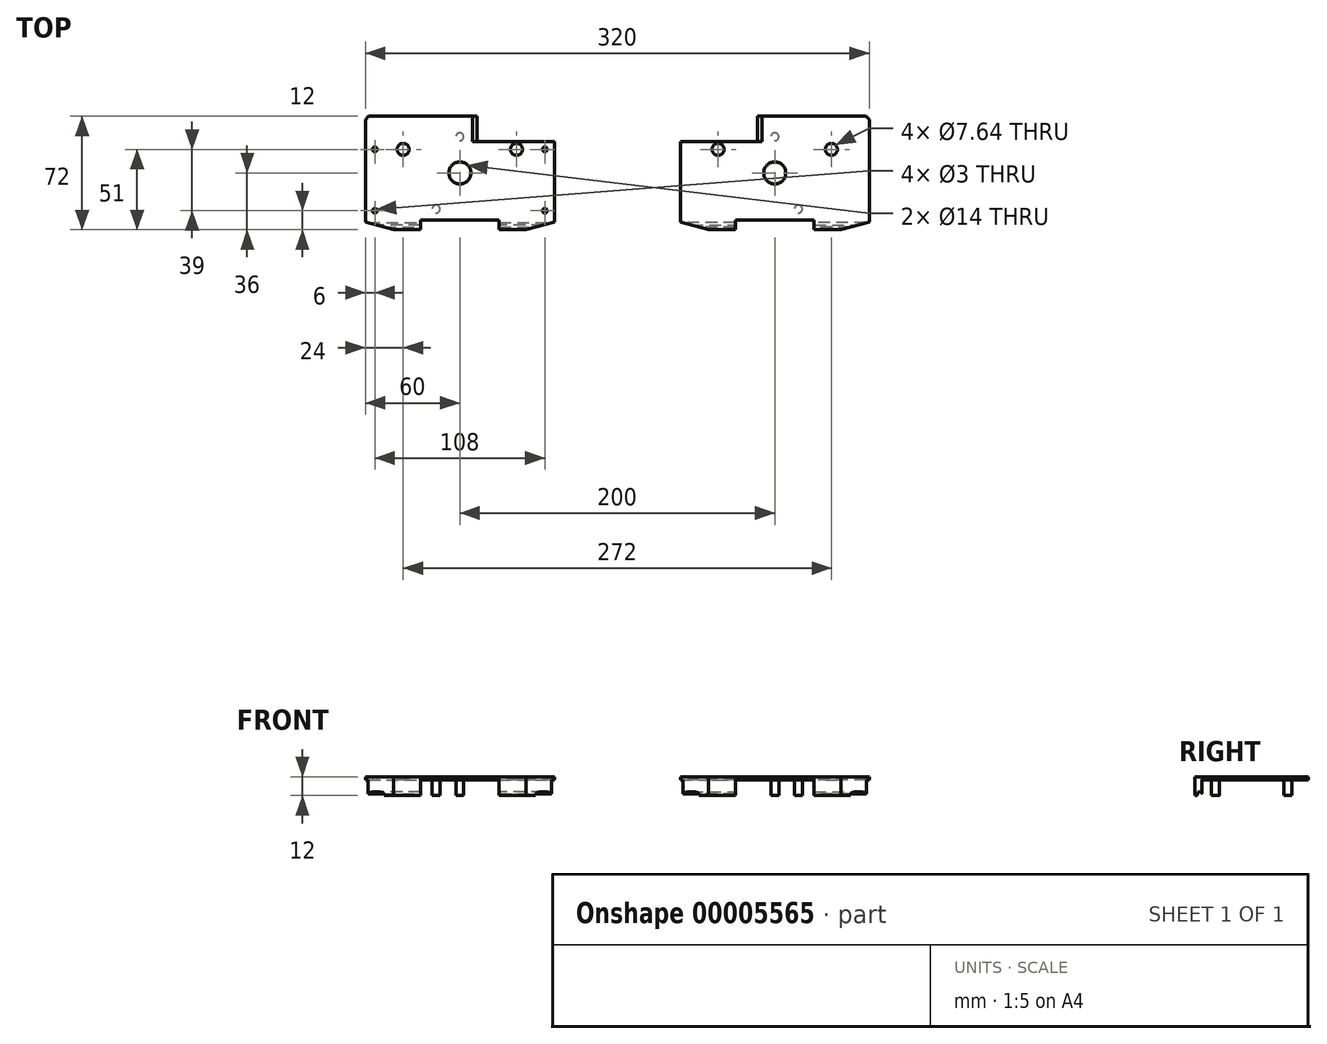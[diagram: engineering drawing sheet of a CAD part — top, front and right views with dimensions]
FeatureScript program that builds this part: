
annotation { "Feature Type Name" : "Feature", "Feature Type Description" : "" }
export const myFeature = defineFeature(function(context is Context, id is Id, definition is map)
    precondition{}
    {
        {
            var Q0;
            Q0=qCreatedBy(makeId("Top.planeOp"),FACE);
            var sketch = newSketch(context, id + "F0", { "sketchPlane" : qUnion([Q0])});
            skLineSegment(sketch, "E0.bottom", {"start": v(-60, 36) * mm, "end": v(60, 36) * mm});
            skLineSegment(sketch, "E0.top", {"start": v(-60, -36) * mm, "end": v(60, -36) * mm});
            skLineSegment(sketch, "E0.left", {"start": v(-60, 36) * mm, "end": v(-60, -36) * mm, "construction": true});
            skLineSegment(sketch, "E0.right", {"start": v(60, 36) * mm, "end": v(60, -36) * mm, "construction": true});
            skCircle(sketch, "E1", {"center": v(0, 0) * mm, "radius": 7 * mm});
            skLineSegment(sketch, "E2", {"start": v(-60, 0) * mm, "end": v(60, 0) * mm, "construction": true});
            skCircle(sketch, "E3", {"center": v(0, 23) * mm, "radius": 2.4 * mm, "construction": true});
            skCircle(sketch, "E4.0.MirrorC", {"center": v(0, -23) * mm, "radius": 2.4 * mm, "construction": true});
            skCircle(sketch, "E5.0.MirrorC", {"center": v(-15, 23) * mm, "radius": 2.5 * mm, "construction": true});
            skCircle(sketch, "E6.0.MirrorC", {"center": v(-15, -23) * mm, "radius": 2.5 * mm, "construction": true});
            skLineSegment(sketch, "E7.bottom", {"start": v(-22.32, 36) * mm, "end": v(10.24, 36) * mm, "construction": true});
            skLineSegment(sketch, "E7.top", {"start": v(-23.32, -36) * mm, "end": v(9.24, -36) * mm, "construction": true});
            skLineSegment(sketch, "E8.left", {"start": v(-60, 36) * mm, "end": v(-60, -36) * mm});
            skLineSegment(sketch, "E8.right", {"start": v(60, 36) * mm, "end": v(60, -36) * mm});
            skLineSegment(sketch, "E9.bottom", {"start": v(-60, 36) * mm, "end": v(-42, 36) * mm, "construction": true});
            skLineSegment(sketch, "E9.top", {"start": v(-60, -36) * mm, "end": v(-42, -36) * mm, "construction": true});
            skLineSegment(sketch, "E9.right", {"start": v(-42, 36) * mm, "end": v(-42, -36) * mm, "construction": true});
            skCircle(sketch, "E10", {"center": v(-36, 15) * mm, "radius": 3.82 * mm});
            skCircle(sketch, "E11.0.MirrorC", {"center": v(36, 15) * mm, "radius": 3.82 * mm});
            skLineSegment(sketch, "E12.bottom", {"start": v(10, -36) * mm, "end": v(-10, -36) * mm});
            skLineSegment(sketch, "E13", {"start": v(0, 23) * mm, "end": v(0, -23) * mm, "construction": true});
            skLineSegment(sketch, "E14", {"start": v(-36, 15) * mm, "end": v(0, 15) * mm, "construction": true});
            skLineSegment(sketch, "E15", {"start": v(0, 15) * mm, "end": v(36, 15) * mm, "construction": true});
            skCircle(sketch, "E16", {"center": v(-54, -24) * mm, "radius": 1.5 * mm, "construction": true});
            skCircle(sketch, "E17", {"center": v(-54, 15) * mm, "radius": 1.5 * mm, "construction": true});
            skLineSegment(sketch, "E18", {"start": v(-36, 15) * mm, "end": v(-56.54, 15) * mm, "construction": true});
            skLineSegment(sketch, "E19", {"start": v(-54, -24) * mm, "end": v(-54, 15) * mm, "construction": true});
            skCircle(sketch, "E20.0.MirrorC", {"center": v(54, 15) * mm, "radius": 1.5 * mm, "construction": true});
            skCircle(sketch, "E21.0.MirrorC", {"center": v(54, -24) * mm, "radius": 1.5 * mm, "construction": true});
            skSolve(sketch);
        }
        {
            var Q0;
            Q0=makeQuery(id+"F0.imprint","IMPRINT",FACE,{"disambiguationData":[TD([[makeQuery(id+"F0.imprint","IMPRINT",EDGE,{"derivedFrom":sQuery(id+"F0.wireOp",EDGE,"E1")}),-1.0]])]});
            extrude(context, id + "F1", {"entities" : qUnion([Q0]), "depth" : 12 * mm});
        }
        {
            var Q0;
            Q0=makeQuery(id+"F1.opExtrude","CAP_FACE",FACE,{"disambiguationData":[OSD([sQuery(id+"F0.wireOp",EDGE,"E1"),sQuery(id+"F0.wireOp",EDGE,"E0.bottom"),sQuery(id+"F0.wireOp",EDGE,"E0.top"),sQuery(id+"F0.wireOp",EDGE,"E8.left"),sQuery(id+"F0.wireOp",EDGE,"E8.right"),sQuery(id+"F0.wireOp",EDGE,"E10"),sQuery(id+"F0.wireOp",EDGE,"E11.0.MirrorC"),sQuery(id+"F0.wireOp",EDGE,"E12.bottom")])],"isStart":false});
            var sketch = newSketch(context, id + "F2", { "sketchPlane" : qUnion([Q0])});
            skLineSegment(sketch, "E22", {"start": v(60, 20) * mm, "end": v(60, 36) * mm});
            skLineSegment(sketch, "E23", {"start": v(60, 36) * mm, "end": v(-42, 36) * mm});
            skLineSegment(sketch, "E24", {"start": v(-60, -36) * mm, "end": v(60, -36) * mm});
            skLineSegment(sketch, "E25", {"start": v(-42, 20) * mm, "end": v(60, 20) * mm});
            skLineSegment(sketch, "E26", {"start": v(60, -36) * mm, "end": v(-60, -36) * mm});
            skLineSegment(sketch, "E27", {"start": v(-60, 36) * mm, "end": v(-42, 36) * mm, "construction": true});
            skLineSegment(sketch, "E28", {"start": v(60, 36) * mm, "end": v(60, 20) * mm});
            skLineSegment(sketch, "E29", {"start": v(-42, 36) * mm, "end": v(-42, 27) * mm, "construction": true});
            skLineSegment(sketch, "E30", {"start": v(-42, 27) * mm, "end": v(-46, 27) * mm, "construction": true});
            skLineSegment(sketch, "E31", {"start": v(-46, 27) * mm, "end": v(-46, 20) * mm, "construction": true});
            skLineSegment(sketch, "E32", {"start": v(-46, 20) * mm, "end": v(-42, 20) * mm, "construction": true});
            skSolve(sketch);
        }
        {
            var Q0;
            Q0=makeQuery(id+"F0.imprint","IMPRINT",FACE,{"disambiguationData":[TD([[makeQuery(id+"F0.imprint","IMPRINT",EDGE,{"derivedFrom":sQuery(id+"F0.wireOp",EDGE,"E1")}),-1.0]])]});
            var sketch = newSketch(context, id + "F3", { "sketchPlane" : qUnion([Q0])});
            skLineSegment(sketch, "E33.bottom", {"start": v(25, -36) * mm, "end": v(-25, -36) * mm});
            skLineSegment(sketch, "E33.top", {"start": v(25, -30) * mm, "end": v(-25, -30) * mm});
            skLineSegment(sketch, "E33.left", {"start": v(25, -36) * mm, "end": v(25, -30) * mm});
            skLineSegment(sketch, "E33.right", {"start": v(-25, -36) * mm, "end": v(-25, -30) * mm});
            skLineSegment(sketch, "E34", {"start": v(-25, -33) * mm, "end": v(0, -33) * mm, "construction": true});
            skLineSegment(sketch, "E35", {"start": v(0, -33) * mm, "end": v(25, -33) * mm, "construction": true});
            skLineSegment(sketch, "E36", {"start": v(0, -22.48) * mm, "end": v(0, -36) * mm, "construction": true});
            skSolve(sketch);
        }
        {
            var Q0;
            Q0=makeQuery(id+"F3.imprint","IMPRINT",FACE,{"disambiguationData":[TD([[makeQuery(id+"F3.imprint","IMPRINT",EDGE,{"derivedFrom":sQuery(id+"F3.wireOp",EDGE,"E33.top")}),1.0]])]});
            var Q1;
            Q1=makeQuery(id+"F1.opExtrude","CAP_FACE",FACE,{"disambiguationData":[OSD([sQuery(id+"F0.wireOp",EDGE,"E1"),sQuery(id+"F0.wireOp",EDGE,"E0.bottom"),sQuery(id+"F0.wireOp",EDGE,"E0.top"),sQuery(id+"F0.wireOp",EDGE,"E8.left"),sQuery(id+"F0.wireOp",EDGE,"E8.right"),sQuery(id+"F0.wireOp",EDGE,"E10"),sQuery(id+"F0.wireOp",EDGE,"E11.0.MirrorC"),sQuery(id+"F0.wireOp",EDGE,"E12.bottom")])],"isStart":false});
            extrude(context, id + "F4", {"entities" : qUnion([Q0]), "operationType" : NewBodyOperationType.REMOVE, "endBound" : BoundingType.UP_TO_SURFACE, "endBoundEntityFace" : qUnion([Q1]), "depth" : 25 * mm});
        }
        {
            var Q0;
            Q0=makeQuery(id+"F0.imprint","IMPRINT",FACE,{"disambiguationData":[TD([[makeQuery(id+"F0.imprint","IMPRINT",EDGE,{"derivedFrom":sQuery(id+"F0.wireOp",EDGE,"E1")}),-1.0]])]});
            var sketch = newSketch(context, id + "F5", { "sketchPlane" : qUnion([Q0])});
            skLineSegment(sketch, "E37.bottom", {"start": v(-60, -31.62) * mm, "end": v(60, -31.63) * mm});
            skLineSegment(sketch, "E37.top", {"start": v(-60, -34.37) * mm, "end": v(60, -34.38) * mm});
            skLineSegment(sketch, "E37.left", {"start": v(-60, -31.62) * mm, "end": v(-60, -34.37) * mm});
            skLineSegment(sketch, "E37.right", {"start": v(60, -31.63) * mm, "end": v(60, -34.38) * mm});
            skLineSegment(sketch, "E38", {"start": v(8.47, -31.63) * mm, "end": v(8.47, -30) * mm, "construction": true});
            skLineSegment(sketch, "E39", {"start": v(8.43, -34.38) * mm, "end": v(8.43, -36) * mm, "construction": true});
            skSolve(sketch);
        }
        {
            var Q0;
            Q0=makeQuery(id+"F5.imprint","IMPRINT",FACE,{"disambiguationData":[TD([[makeQuery(id+"F5.imprint","IMPRINT",EDGE,{"derivedFrom":sQuery(id+"F5.wireOp",EDGE,"E37.bottom")}),-1.0]])]});
            extrude(context, id + "F6", {"entities" : qUnion([Q0]), "operationType" : NewBodyOperationType.REMOVE, "depth" : 2.5 * mm});
        }
        {
            var Q0;
            Q0=makeQuery(id+"F6.boolean.opBoolean","COPY",EDGE,{"disambiguationData":[OD(1.0)],"derivedFrom":makeQuery(id+"F6.opExtrude","CAP_EDGE",EDGE,{"disambiguationData":[OSD([sQuery(id+"F5.wireOp",EDGE,"E37.bottom")])],"isStart":false})});
            var Q1;
            Q1=makeQuery(id+"F6.boolean.opBoolean","COPY",EDGE,{"disambiguationData":[OD(1.0)],"derivedFrom":makeQuery(id+"F6.opExtrude","CAP_EDGE",EDGE,{"disambiguationData":[OSD([sQuery(id+"F5.wireOp",EDGE,"E37.top")])],"isStart":false})});
            var Q2;
            Q2=makeQuery(id+"F6.boolean.opBoolean","COPY",EDGE,{"disambiguationData":[OD(0.0)],"derivedFrom":makeQuery(id+"F6.opExtrude","CAP_EDGE",EDGE,{"disambiguationData":[OSD([sQuery(id+"F5.wireOp",EDGE,"E37.top")])],"isStart":false})});
            var Q3;
            Q3=makeQuery(id+"F6.boolean.opBoolean","COPY",EDGE,{"disambiguationData":[OD(0.0)],"derivedFrom":makeQuery(id+"F6.opExtrude","CAP_EDGE",EDGE,{"disambiguationData":[OSD([sQuery(id+"F5.wireOp",EDGE,"E37.bottom")])],"isStart":false})});
            fillet(context, id + "F7", {"entities" : qUnion([Q0, Q1, Q2, Q3]), "radius" : 1.5 * mm, "tangentPropagation" : true, "allowEdgeOverflow" : false});
        }
        {
            var Q0;
            Q0=makeQuery(id+"F1.opExtrude","SWEPT_FACE",FACE,{"disambiguationData":[OSD([sQuery(id+"F0.wireOp",EDGE,"E0.bottom")])]});
            var sketch = newSketch(context, id + "F8", { "sketchPlane" : qUnion([Q0])});
            skLineSegment(sketch, "E40", {"start": v(-60, 6) * mm, "end": v(-38.5, 6) * mm, "construction": true});
            skLineSegment(sketch, "E41", {"start": v(0, 0) * mm, "end": v(0, 12) * mm, "construction": true});
            skLineSegment(sketch, "E42", {"start": v(-8, 0) * mm, "end": v(-8, 12) * mm, "construction": true});
            skLineSegment(sketch, "E43", {"start": v(-8, 12) * mm, "end": v(-60, 12) * mm});
            skLineSegment(sketch, "E44", {"start": v(-60, 2) * mm, "end": v(-60, 12) * mm});
            skLineSegment(sketch, "E45", {"start": v(-8, 2) * mm, "end": v(-23.25, 2) * mm, "construction": true});
            skLineSegment(sketch, "E46", {"start": v(-23.25, 2) * mm, "end": v(-38.5, 2) * mm, "construction": true});
            skLineSegment(sketch, "E47", {"start": v(-38.5, 6) * mm, "end": v(-38.5, 0) * mm, "construction": true});
            skLineSegment(sketch, "E48", {"start": v(-60, 2) * mm, "end": v(-23.25, 2) * mm});
            skLineSegment(sketch, "E49", {"start": v(-23.25, 2) * mm, "end": v(-8, 12) * mm});
            skSolve(sketch);
        }
        {
            var Q0;
            Q0=makeQuery(id+"F8.imprint","IMPRINT",FACE,{"disambiguationData":[TD([[makeQuery(id+"F8.imprint","IMPRINT",EDGE,{"derivedFrom":sQuery(id+"F8.wireOp",EDGE,"E43")}),1.0]])]});
            extrude(context, id + "F9", {"entities" : qUnion([Q0]), "operationType" : NewBodyOperationType.REMOVE, "oppositeDirection" : true, "depth" : 16 * mm});
        }
        {
            var Q0;
            Q0=makeQuery(id+"F9.boolean.opBoolean","COPY",EDGE,{"derivedFrom":makeQuery(id+"F9.opExtrude","SWEPT_EDGE",EDGE,{"disambiguationData":[OSD([sQuery(id+"F8.wireOp",EDGE,"dc820323-19ea-4039-b468-714fe8b4bf2b"),sQuery(id+"F8.wireOp",EDGE,"f9c62189-2ec5-4655-88e0-a14efa9e9823")])]})});
            var Q1;
            Q1=makeQuery(id+"F9.boolean.opBoolean","COPY",EDGE,{"derivedFrom":makeQuery(id+"F9.opExtrude","SWEPT_EDGE",EDGE,{"disambiguationData":[OSD([sQuery(id+"F2.wireOp",EDGE,"E23"),sQuery(id+"F8.wireOp",EDGE,"f9c62189-2ec5-4655-88e0-a14efa9e9823"),sQuery(id+"F8.wireOp",EDGE,"E43")])]})});
            var Q2;
            Q2=makeQuery(id+"F9.boolean.opBoolean","COPY",EDGE,{"derivedFrom":makeQuery(id+"F9.opExtrude","SWEPT_EDGE",EDGE,{"disambiguationData":[OSD([sQuery(id+"F8.wireOp",EDGE,"E48"),sQuery(id+"F8.wireOp",EDGE,"E49")])]})});
            var Q3;
            Q3=makeQuery(id+"F9.boolean.opBoolean","COPY",EDGE,{"derivedFrom":makeQuery(id+"F9.opExtrude","SWEPT_EDGE",EDGE,{"disambiguationData":[OSD([sQuery(id+"F0.wireOp",EDGE,"E0.bottom"),sQuery(id+"F8.wireOp",EDGE,"E43"),sQuery(id+"F8.wireOp",EDGE,"E49")])]})});
            fillet(context, id + "F10", {"entities" : qUnion([Q0, Q1, Q2, Q3]), "radius" : 5 * mm, "tangentPropagation" : true, "allowEdgeOverflow" : false});
        }
        {
            var Q0;
            {var subQ0=sQuery(id+"F0.wireOp",EDGE,"E1");var subQ1=sQuery(id+"F0.wireOp",EDGE,"E0.bottom");var subQ2=sQuery(id+"F0.wireOp",EDGE,"E8.left");var subQ3=sQuery(id+"F0.wireOp",EDGE,"E8.right");var subQ4=sQuery(id+"F0.wireOp",EDGE,"E10");var subQ5=sQuery(id+"F0.wireOp",EDGE,"E11.0.MirrorC");Q0=makeQuery(id+"F6.boolean.opBoolean","SPLIT",FACE,{"disambiguationData":[TD([makeQuery(id+"F1.opExtrude","SWEPT_FACE",FACE,{"disambiguationData":[OSD([subQ0])]}),makeQuery(id+"F1.opExtrude","SWEPT_FACE",FACE,{"disambiguationData":[OSD([subQ1])]}),makeQuery(id+"F1.opExtrude","SWEPT_FACE",FACE,{"disambiguationData":[OSD([subQ2])]}),makeQuery(id+"F1.opExtrude","SWEPT_FACE",FACE,{"disambiguationData":[OSD([subQ3])]}),makeQuery(id+"F1.opExtrude","SWEPT_FACE",FACE,{"disambiguationData":[OSD([subQ4])]}),makeQuery(id+"F1.opExtrude","SWEPT_FACE",FACE,{"disambiguationData":[OSD([subQ5])]}),makeQuery(id+"F4.boolean.opBoolean","COPY",FACE,{"derivedFrom":makeQuery(id+"F4.opExtrude","SWEPT_FACE",FACE,{"disambiguationData":[OSD([sQuery(id+"F3.wireOp",EDGE,"E33.top")])]})}),makeQuery(id+"F4.boolean.opBoolean","COPY",FACE,{"derivedFrom":makeQuery(id+"F4.opExtrude","SWEPT_FACE",FACE,{"disambiguationData":[OSD([sQuery(id+"F3.wireOp",EDGE,"E33.left")])]})}),makeQuery(id+"F4.boolean.opBoolean","COPY",FACE,{"derivedFrom":makeQuery(id+"F4.opExtrude","SWEPT_FACE",FACE,{"disambiguationData":[OSD([sQuery(id+"F3.wireOp",EDGE,"E33.right")])]})}),makeQuery(id+"F6.opExtrude","SWEPT_FACE",FACE,{"disambiguationData":[OSD([sQuery(id+"F5.wireOp",EDGE,"E37.bottom")])]})])],"derivedFrom":makeQuery(id+"F1.opExtrude","CAP_FACE",FACE,{"disambiguationData":[OSD([subQ0,subQ1,sQuery(id+"F0.wireOp",EDGE,"E0.top"),subQ2,subQ3,subQ4,subQ5,sQuery(id+"F0.wireOp",EDGE,"E12.bottom")])],"isStart":true})});}
            var sketch = newSketch(context, id + "F11", { "sketchPlane" : qUnion([Q0])});
            skCircle(sketch, "E50", {"center": v(-15.05, -22.91) * mm, "radius": 2.5 * mm});
            skCircle(sketch, "E51.0.MirrorC", {"center": v(-0.05, -23) * mm, "radius": 2.5 * mm});
            skCircle(sketch, "E52.0.MirrorC", {"center": v(-15.05, 22.91) * mm, "radius": 2.5 * mm});
            skCircle(sketch, "E53.0.MirrorC", {"center": v(-0.05, 23) * mm, "radius": 2.5 * mm});
            skSolve(sketch);
        }
        {
            var Q0;
            {Q0=qUnion([makeQuery(id+"F11.imprint","IMPRINT",FACE,{"disambiguationData":[TD([[makeQuery(id+"F11.imprint","IMPRINT",EDGE,{"derivedFrom":sQuery(id+"F11.wireOp",EDGE,"E50")}),1.0]])]}),makeQuery(id+"F11.imprint","IMPRINT",FACE,{"disambiguationData":[TD([[makeQuery(id+"F11.imprint","IMPRINT",EDGE,{"derivedFrom":sQuery(id+"F11.wireOp",EDGE,"E51.0.MirrorC")}),-1.0]])]}),makeQuery(id+"F11.imprint","IMPRINT",FACE,{"disambiguationData":[TD([[makeQuery(id+"F11.imprint","IMPRINT",EDGE,{"derivedFrom":sQuery(id+"F11.wireOp",EDGE,"E52.0.MirrorC")}),-1.0]])]}),makeQuery(id+"F11.imprint","IMPRINT",FACE,{"disambiguationData":[TD([[makeQuery(id+"F11.imprint","IMPRINT",EDGE,{"derivedFrom":sQuery(id+"F11.wireOp",EDGE,"E53.0.MirrorC")}),1.0]])]})]);}
            extrude(context, id + "F12", {"entities" : qUnion([Q0]), "operationType" : NewBodyOperationType.REMOVE, "oppositeDirection" : true, "depth" : 10 * mm});
        }
        {
            var Q0;
            Q0=makeQuery(id+"F0.imprint","IMPRINT",FACE,{"disambiguationData":[TD([[makeQuery(id+"F0.imprint","IMPRINT",EDGE,{"derivedFrom":sQuery(id+"F0.wireOp",EDGE,"E1")}),-1.0]])]});
            var sketch = newSketch(context, id + "F13", { "sketchPlane" : qUnion([Q0])});
            skLineSegment(sketch, "E54", {"start": v(-60, -31.12) * mm, "end": v(-42, -36) * mm});
            skLineSegment(sketch, "E55", {"start": v(-42, -36) * mm, "end": v(-60, -36) * mm});
            skLineSegment(sketch, "E56", {"start": v(-60, -36) * mm, "end": v(-60, -31.12) * mm});
            skPoint(sketch, "E57", {"position": v(-60, -31.62) * mm});
            skLineSegment(sketch, "E58.MirrorCS", {"start": v(60, -31.12) * mm, "end": v(42, -36) * mm});
            skLineSegment(sketch, "E59.MirrorCS", {"start": v(60, -36) * mm, "end": v(60, -31.12) * mm});
            skLineSegment(sketch, "E60.MirrorCS", {"start": v(42, -36) * mm, "end": v(60, -36) * mm});
            skSolve(sketch);
        }
        {
            var Q0;
            Q0 = qSketchRegion(id + "F13", true);
            var Q1;
            Q1=makeQuery(id+"F1.opExtrude","CAP_FACE",FACE,{"disambiguationData":[OSD([sQuery(id+"F0.wireOp",EDGE,"E1"),sQuery(id+"F0.wireOp",EDGE,"E0.bottom"),sQuery(id+"F0.wireOp",EDGE,"E0.top"),sQuery(id+"F0.wireOp",EDGE,"E8.left"),sQuery(id+"F0.wireOp",EDGE,"E8.right"),sQuery(id+"F0.wireOp",EDGE,"E10"),sQuery(id+"F0.wireOp",EDGE,"E11.0.MirrorC"),sQuery(id+"F0.wireOp",EDGE,"E12.bottom")])],"isStart":false});
            extrude(context, id + "F14", {"entities" : qUnion([Q0]), "operationType" : NewBodyOperationType.REMOVE, "endBound" : BoundingType.UP_TO_SURFACE, "endBoundEntityFace" : qUnion([Q1]), "depth" : 25 * mm});
        }
        {
            var Q0;
            Q0=makeQuery(id+"F1.opExtrude","SWEPT_EDGE",EDGE,{"disambiguationData":[OSD([sQuery(id+"F0.wireOp",EDGE,"E0.bottom"),sQuery(id+"F0.wireOp",EDGE,"E8.left")])]});
            chamfer(context, id + "F15", {"entities" : qUnion([Q0]), "width" : 2 * mm, "tangentPropagation" : true});
        }
        {
            var Q0;
            Q0=qCreatedBy(makeId("Right.planeOp"),FACE);
            cPlane(context, id + "F16", {"entities" : qUnion([Q0]), "cplaneType" : CPlaneType.OFFSET, "offset" : 100 * mm, "width" : 150 * mm, "height" : 150 * mm});
        }
        {
            var Q0;
            Q0=makeQuery(id+"F1.opExtrude","SWEPT_BODY",BODY,{"disambiguationData":[OSD([sQuery(id+"F0.wireOp",EDGE,"E1"),sQuery(id+"F0.wireOp",EDGE,"E0.bottom"),sQuery(id+"F0.wireOp",EDGE,"E0.top"),sQuery(id+"F0.wireOp",EDGE,"E8.left"),sQuery(id+"F0.wireOp",EDGE,"E8.right"),sQuery(id+"F0.wireOp",EDGE,"E10"),sQuery(id+"F0.wireOp",EDGE,"E11.0.MirrorC"),sQuery(id+"F0.wireOp",EDGE,"E12.bottom")])]});
            var Q1;
            Q1=qCreatedBy(id+"F16.planeOp",FACE);
            mirror(context, id + "F17", {"entities" : qUnion([Q0]), "mirrorPlane" : qUnion([Q1])});
        }
        {
            var Q0;
            Q0=qCreatedBy(makeId("Top.planeOp"),FACE);
            var sketch = newSketch(context, id + "F18", { "sketchPlane" : qUnion([Q0])});
            skCircle(sketch, "E61", {"center": v(-54, -24) * mm, "radius": 1.5 * mm});
            skCircle(sketch, "E62", {"center": v(-54, 15) * mm, "radius": 1.5 * mm});
            skCircle(sketch, "E63", {"center": v(54, 15) * mm, "radius": 1.5 * mm});
            skCircle(sketch, "E64", {"center": v(54, -24) * mm, "radius": 1.5 * mm});
            skSolve(sketch);
        }
        {
            var Q0;
            {Q0=qUnion([makeQuery(id+"F18.imprint","IMPRINT",FACE,{"disambiguationData":[TD([[makeQuery(id+"F18.imprint","IMPRINT",EDGE,{"derivedFrom":sQuery(id+"F18.wireOp",EDGE,"E61")}),1.0]])]}),makeQuery(id+"F18.imprint","IMPRINT",FACE,{"disambiguationData":[TD([[makeQuery(id+"F18.imprint","IMPRINT",EDGE,{"derivedFrom":sQuery(id+"F18.wireOp",EDGE,"E62")}),1.0]])]}),makeQuery(id+"F18.imprint","IMPRINT",FACE,{"disambiguationData":[TD([[makeQuery(id+"F18.imprint","IMPRINT",EDGE,{"derivedFrom":sQuery(id+"F18.wireOp",EDGE,"E63")}),1.0]])]}),makeQuery(id+"F18.imprint","IMPRINT",FACE,{"disambiguationData":[TD([[makeQuery(id+"F18.imprint","IMPRINT",EDGE,{"derivedFrom":sQuery(id+"F18.wireOp",EDGE,"E64")}),1.0]])]})]);}
            var Q1;
            Q1=makeQuery(id+"F1.opExtrude","CAP_FACE",FACE,{"disambiguationData":[OSD([sQuery(id+"F0.wireOp",EDGE,"E1"),sQuery(id+"F0.wireOp",EDGE,"E0.bottom"),sQuery(id+"F0.wireOp",EDGE,"E0.top"),sQuery(id+"F0.wireOp",EDGE,"E8.left"),sQuery(id+"F0.wireOp",EDGE,"E8.right"),sQuery(id+"F0.wireOp",EDGE,"E10"),sQuery(id+"F0.wireOp",EDGE,"E11.0.MirrorC"),sQuery(id+"F0.wireOp",EDGE,"E12.bottom")])],"isStart":false});
            extrude(context, id + "F19", {"entities" : qUnion([Q0]), "operationType" : NewBodyOperationType.REMOVE, "endBound" : BoundingType.UP_TO_SURFACE, "endBoundEntityFace" : qUnion([Q1]), "depth" : 25 * mm});
        }
        {
            var Q0;
            Q0=qCreatedBy(makeId("Top.planeOp"),FACE);
            var sketch = newSketch(context, id + "F20", { "sketchPlane" : qUnion([Q0])});
            skCircle(sketch, "E65", {"center": v(-54, -24) * mm, "radius": 3 * mm});
            skCircle(sketch, "E66", {"center": v(-54, 15) * mm, "radius": 3 * mm});
            skCircle(sketch, "E67", {"center": v(54, 15) * mm, "radius": 3 * mm});
            skCircle(sketch, "E68", {"center": v(54, -24) * mm, "radius": 3 * mm});
            skSolve(sketch);
        }
        {
            var Q0;
            {Q0=qUnion([makeQuery(id+"F20.imprint","IMPRINT",FACE,{"disambiguationData":[TD([[makeQuery(id+"F20.imprint","IMPRINT",EDGE,{"derivedFrom":sQuery(id+"F20.wireOp",EDGE,"E65")}),1.0]])]}),makeQuery(id+"F20.imprint","IMPRINT",FACE,{"disambiguationData":[TD([[makeQuery(id+"F20.imprint","IMPRINT",EDGE,{"derivedFrom":sQuery(id+"F20.wireOp",EDGE,"E66")}),1.0]])]}),makeQuery(id+"F20.imprint","IMPRINT",FACE,{"disambiguationData":[TD([[makeQuery(id+"F20.imprint","IMPRINT",EDGE,{"derivedFrom":sQuery(id+"F20.wireOp",EDGE,"E67")}),1.0]])]}),makeQuery(id+"F20.imprint","IMPRINT",FACE,{"disambiguationData":[TD([[makeQuery(id+"F20.imprint","IMPRINT",EDGE,{"derivedFrom":sQuery(id+"F20.wireOp",EDGE,"E68")}),1.0]])]})]);}
            extrude(context, id + "F21", {"entities" : qUnion([Q0]), "operationType" : NewBodyOperationType.REMOVE, "depth" : 3 * mm});
        }
    });
